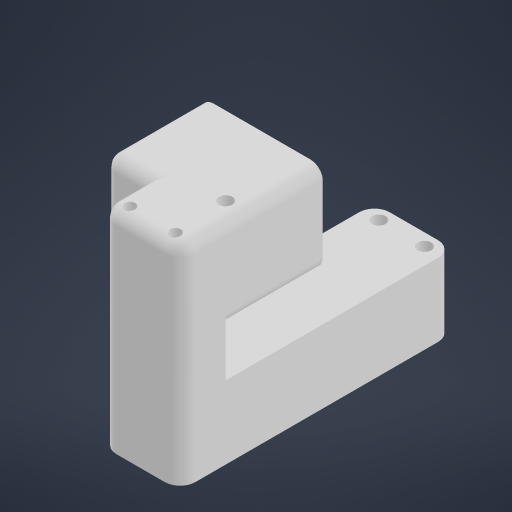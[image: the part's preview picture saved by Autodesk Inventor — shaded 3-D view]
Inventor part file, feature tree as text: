
AUTODESK INVENTOR PART (.ipt)
format: ipt  version: 2024.1 (Build 281209000, 209)  size: 380,928 bytes
history: native  units: mm
features: extrude x13, sketch x6, fillet x3, projected_geometry x3
ambient origin geometry x8: Origin, YZ Plane, XZ Plane, XY Plane, X Axis, Y Axis, Z Axis, Center Point
bodies: Solid1 (feature_tree)
feature tree (25):
  sketch  "Sketch1"  dims[d0=22.0mm d1=70.0mm]
  extrude  "Extrusion1"  Depth=70.0mm
  extrude  "Extrusion2"  Depth=2.0mm
  extrude  "Extrusion3"  Depth=15.0mm
  fillet  "Fillet1"  Radius=2.0mm
  sketch  "Sketch2"  dims[d2=2.0mm d3=4.5mm]
  extrude  "Extrusion4"  Depth=8.0mm
  sketch  "Sketch3"  dims[d4=8.0mm d6=15.0mm d7=2.0mm d8=0.0mm]
  extrude  "Extrusion5"  Depth=8.0mm TaperAngle=0.0deg
  extrude  "Extrusion6"  Depth=3.5mm
  sketch  "Sketch5"  dims[d9=22.0mm d10=0.0mm d11=8.0mm]
  extrude  "Extrusion8"  Depth=15.0mm
  extrude  "Extrusion13"  Depth=45.0mm TaperAngle=0.0deg
  extrude  "Extrusion14"  Depth=40.0mm
  extrude  "Extrusion15"  Depth=30.0mm
  extrude  "Extrusion9"  Depth=2.0mm
  extrude  "Extrusion10"  Depth=2.0mm TaperAngle=0.0deg
  extrude  "Extrusion12"  Depth=30.0mm TaperAngle=0.0deg
  fillet  "Fillet2"  Radius=4.5mm
  fillet  "Fillet3"  Radius=2.0mm
  projected_geometry  "Projected Loop1"
  projected_geometry  "Projected Loop2"
  sketch  "Sketch6"  dims[d12=8.0mm d13=34.25mm d14=0.0mm]
  projected_geometry  "Projected Loop3"
  sketch  "Sketch7"  dims[d15=5.0mm d16=3.5mm d17=15.0mm d18=45.0mm d19=0.0mm d23=40.0mm d26=30.0mm d27=2.0mm d28=2.0mm d29=0.0mm d30=30.0mm d31=0.0mm d32=4.5mm d33=2.0mm d36=2.0mm d37=4.5mm d38=10.0mm d39=0.0mm d40=10.0mm d41=0.0mm d42=10.0mm d43=10.0mm d44=0.0mm d47=2.0mm d48=0.0mm d49=4.0mm d50=4.0mm d51=10.0mm d52=0.0mm d53=10.0mm d54=0.0mm d55=30.0mm d56=0.0mm]
